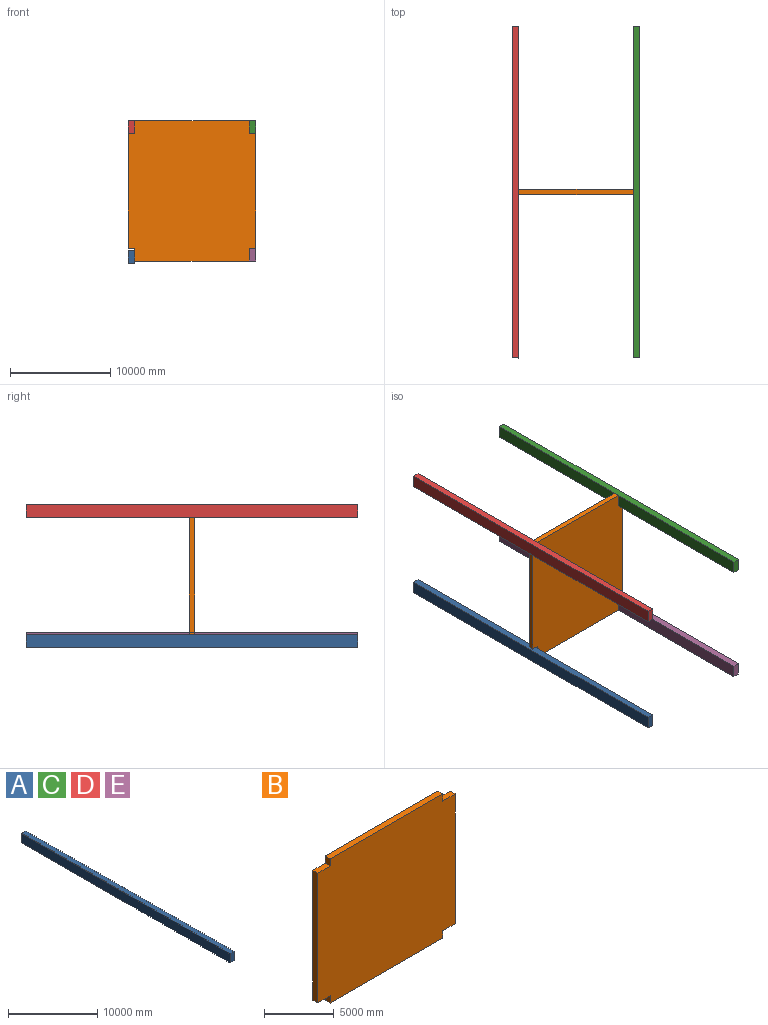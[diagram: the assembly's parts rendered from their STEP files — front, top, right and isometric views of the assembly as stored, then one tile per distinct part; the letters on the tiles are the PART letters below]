
ASSEMBLY  parts=5 mates=7
PART A: 6 faces, bbox 635x33020x1270 mm
  f0: plane 33020x1270mm, normal (-1,0,0), area 41935400mm2, adj f1,f3,f4,f5
  f1: plane 33020x635mm, normal (0,0,-1), area 20967700mm2, adj f0,f2,f4,f5
  f2: plane 33020x1270mm, normal (1,0,0), area 41935400mm2, adj f1,f3,f4,f5
  f3: plane 33020x635mm, normal (0,0,1), area 20967700mm2, adj f0,f2,f4,f5
  f4: plane 1270x635mm, normal (0,-1,0), area 806450mm2, adj f0,f1,f2,f3
  f5: plane 1270x635mm, normal (0,1,0), area 806450mm2, adj f0,f1,f2,f3
PART B: 14 faces, bbox 13970x508x12700 mm
  f0: plane 11430x508mm, normal (-1,0,0), area 5806440mm2, adj f4,f5,f6,f9
  f1: plane 11430x508mm, normal (0,0,-1), area 5806440mm2, adj f4,f5,f8,f10
  f2: plane 11430x508mm, normal (1,0,0), area 5806440mm2, adj f4,f5,f11,f13
  f3: plane 11430x508mm, normal (0,0,1), area 5806440mm2, adj f4,f5,f7,f12
  f4: plane 13970x12700mm, normal (0,-1,0), area 174193200mm2, adj f0,f1,f2,f3,f6,f7,f8,f9
  f5: plane 13970x12700mm, normal (0,1,0), area 174193200mm2, adj f0,f1,f2,f3,f6,f7,f8,f9
  f6: plane 1270x508mm, normal (0,0,1), area 645160mm2, adj f0,f4,f5,f7
  f7: plane 635x508mm, normal (-1,0,0), area 322580mm2, adj f3,f4,f5,f6
  f8: plane 635x508mm, normal (-1,0,0), area 322580mm2, adj f1,f4,f5,f9
  f9: plane 1270x508mm, normal (0,0,-1), area 645160mm2, adj f0,f4,f5,f8
  f10: plane 635x508mm, normal (1,0,0), area 322580mm2, adj f1,f4,f5,f11
  f11: plane 1270x508mm, normal (0,0,-1), area 645160mm2, adj f2,f4,f5,f10
  f12: plane 635x508mm, normal (1,0,0), area 322580mm2, adj f3,f4,f5,f13
  f13: plane 1270x508mm, normal (0,0,1), area 645160mm2, adj f2,f4,f5,f12
PART C: same geometry as A
PART D: same geometry as A
PART E: same geometry as A
PLACE A rot(axis=(-0.8,-0.17,-0.58),0deg) t=(7473.94,-21378.98,18891.41)mm
PLACE B rot(axis=(0,-1,0),90deg) t=(20173.94,-37634.98,19118.52)mm
PLACE C rot(axis=(-0.8,-0.17,-0.58),0deg) t=(19538.94,-21378.98,31818.52)mm
PLACE D rot(axis=(-0.8,-0.17,-0.58),0deg) t=(7473.94,-21378.98,31818.52)mm
PLACE E rot(axis=(-0.8,-0.17,-0.58),0deg) t=(19538.94,-21378.98,19118.52)mm
MATE slider B.f7 <-> A.f3  axis (0,0,-1) through (7791.44,-37888.98,20388.52)mm
MATE slider B.f10 <-> C.f1  axis (0,0,1) through (19856.44,-37888.98,31818.52)mm
MATE slider B.f13 <-> D.f2  axis (-1,0,0) through (8108.94,-37888.98,32453.52)mm
MATE slider B.f12 <-> D.f1  axis (0,0,1) through (7791.44,-37888.98,31818.52)mm
MATE slider B.f8 <-> E.f3  axis (0,0,-1) through (19856.44,-37888.98,20388.52)mm
MATE slider B.f9 <-> E.f0  axis (1,0,0) through (19538.94,-37888.98,19753.52)mm
MATE slider B.f11 <-> C.f0  axis (1,0,0) through (19538.94,-37888.98,32453.52)mm
